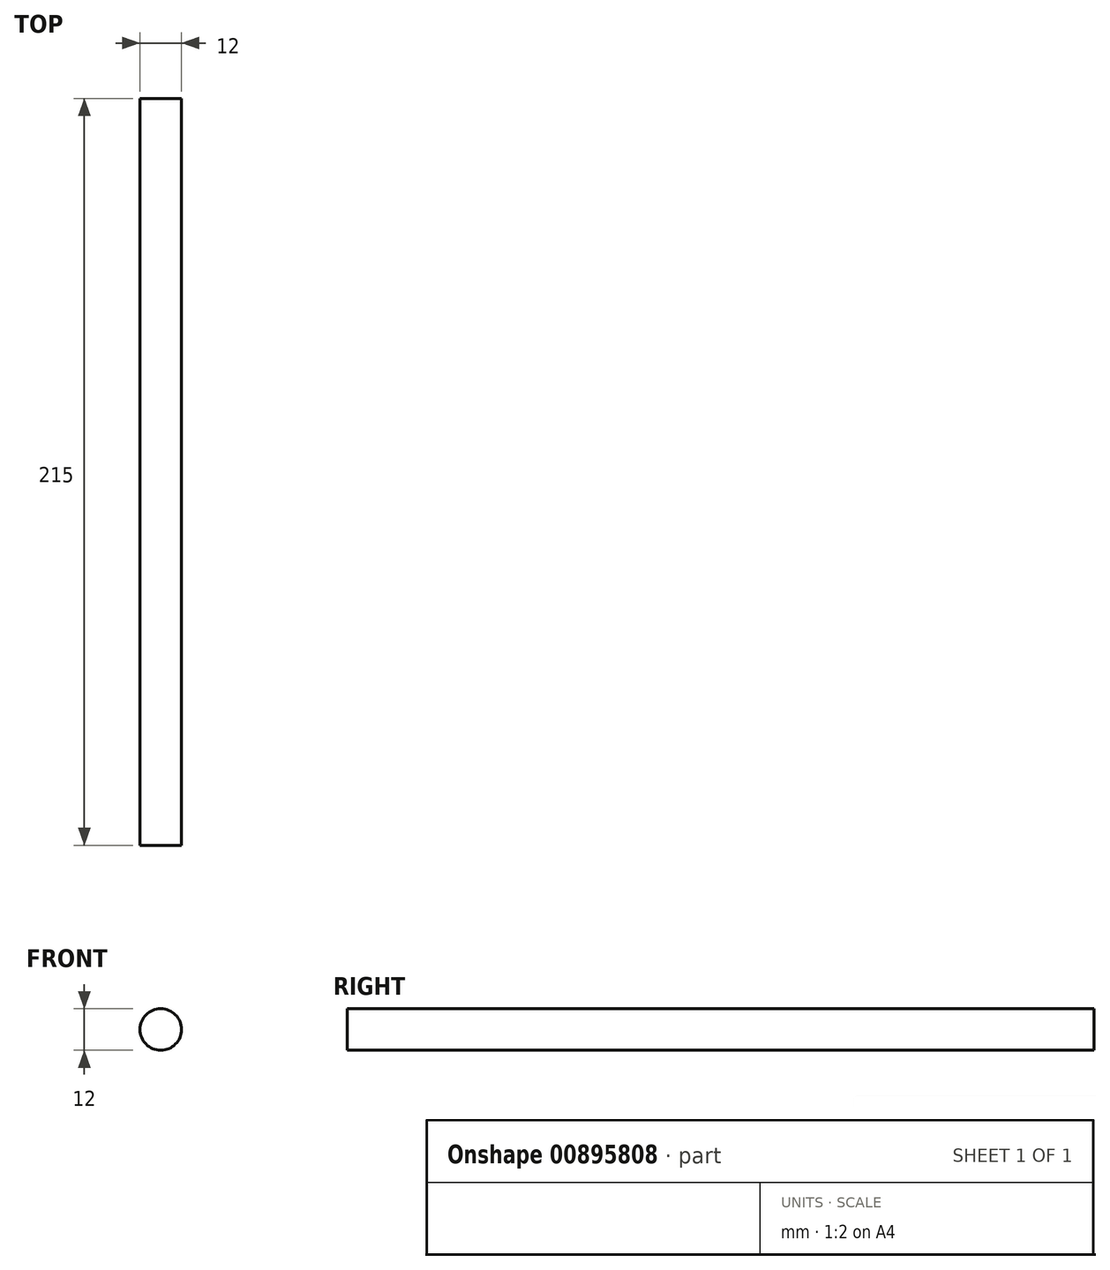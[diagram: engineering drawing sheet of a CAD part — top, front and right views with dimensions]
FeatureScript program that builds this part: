
annotation { "Feature Type Name" : "Feature", "Feature Type Description" : "" }
export const myFeature = defineFeature(function(context is Context, id is Id, definition is map)
    precondition{}
    {
        {
            var Q0;
            Q0=qCreatedBy(makeId("Front.planeOp"),FACE);
            var sketch = newSketch(context, id + "F0", { "sketchPlane" : qUnion([Q0])});
            skCircle(sketch, "E0", {"center": v(0, 0) * mm, "radius": 6 * mm});
            skSolve(sketch);
        }
        {
            var Q0;
            Q0=qSketchRegion(id+"F0",true);
            extrude(context, id + "F1", {"entities" : qUnion([Q0]), "depth" : 215 * mm});
        }
    });
